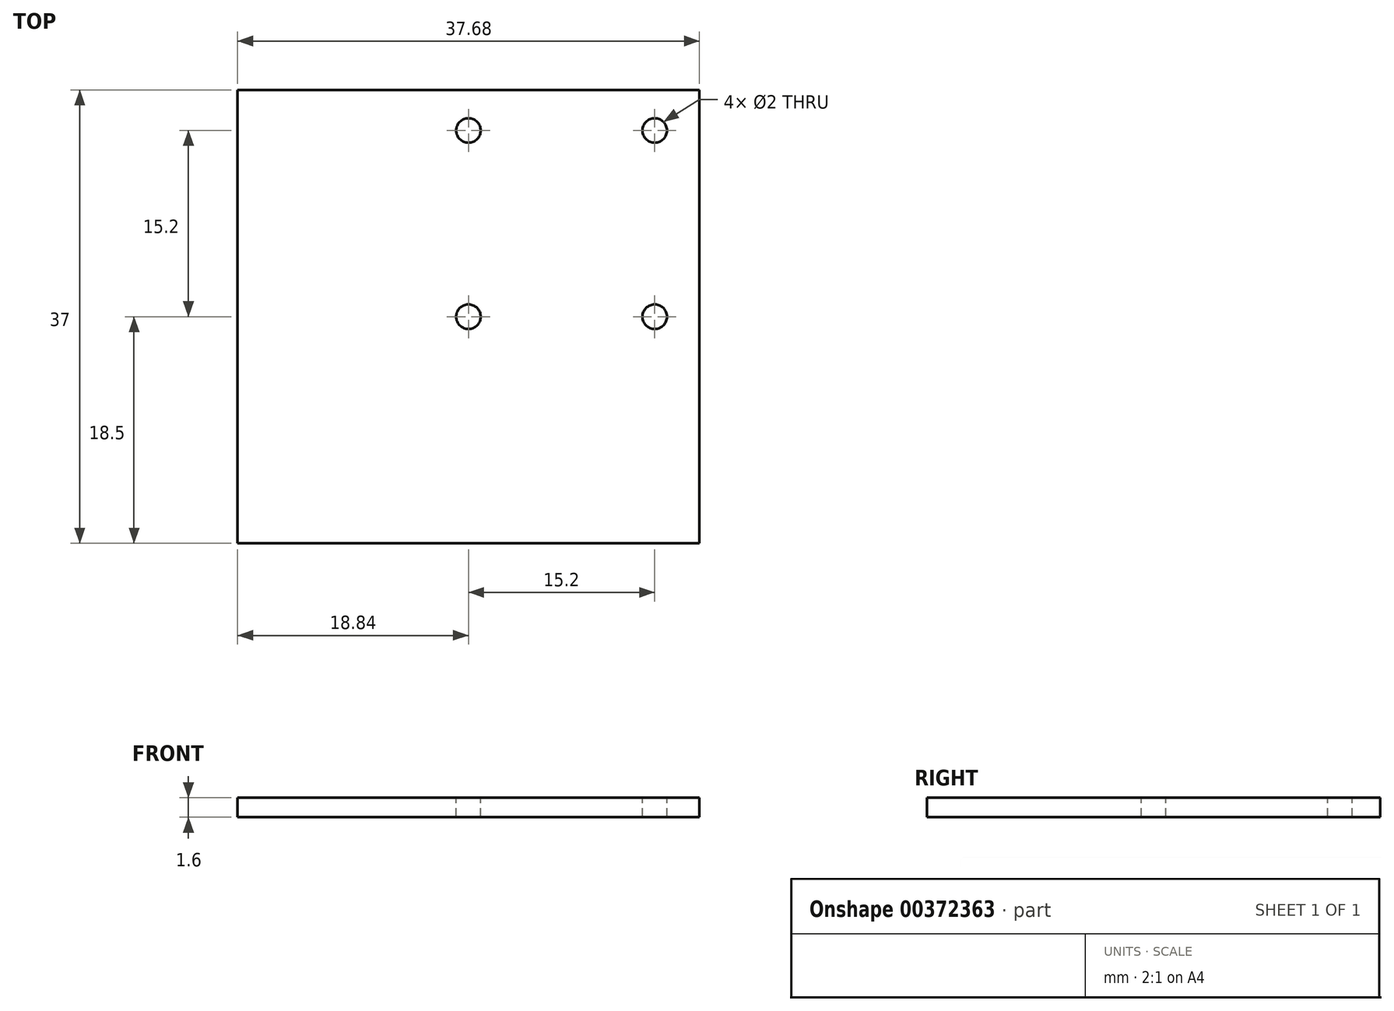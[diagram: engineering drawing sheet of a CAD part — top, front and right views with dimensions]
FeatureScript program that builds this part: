
annotation { "Feature Type Name" : "Feature", "Feature Type Description" : "" }
export const myFeature = defineFeature(function(context is Context, id is Id, definition is map)
    precondition{}
    {
        {
            var Q0;
            Q0=qCreatedBy(makeId("Top.planeOp"),FACE);
            var sketch = newSketch(context, id + "F0", { "sketchPlane" : qUnion([Q0])});
            skLineSegment(sketch, "E0.bottom", {"start": v(18.84, 18.5) * mm, "end": v(-18.84, 18.5) * mm});
            skLineSegment(sketch, "E0.top", {"start": v(18.84, -18.5) * mm, "end": v(-18.84, -18.5) * mm});
            skLineSegment(sketch, "E0.left", {"start": v(18.84, 18.5) * mm, "end": v(18.84, -18.5) * mm});
            skLineSegment(sketch, "E0.right", {"start": v(-18.84, 18.5) * mm, "end": v(-18.84, -18.5) * mm});
            skPoint(sketch, "E0.middle", {"position": v(0, 0) * mm});
            skSolve(sketch);
        }
        {
            var Q0;
            Q0 = qSketchRegion(id + "F0", true);
            extrude(context, id + "F1", {"entities" : qUnion([Q0]), "depth" : 1.6 * mm});
        }
        {
            var Q0;
            Q0=makeQuery(id+"F1.opExtrude","CAP_FACE",FACE,{"disambiguationData":[OSD([sQuery(id+"F0.wireOp",EDGE,"E0.bottom"),sQuery(id+"F0.wireOp",EDGE,"E0.top"),sQuery(id+"F0.wireOp",EDGE,"E0.left"),sQuery(id+"F0.wireOp",EDGE,"E0.right")])],"isStart":false});
            var sketch = newSketch(context, id + "F2", { "sketchPlane" : qUnion([Q0])});
            skCircle(sketch, "E1", {"center": v(0, 0) * mm, "radius": 1 * mm});
            skCircle(sketch, "E2.0.1.0", {"center": v(0, 15.2) * mm, "radius": 1 * mm});
            skCircle(sketch, "E2.1.0.0", {"center": v(15.2, 0) * mm, "radius": 1 * mm});
            skCircle(sketch, "E2.1.1.0", {"center": v(15.2, 15.2) * mm, "radius": 1 * mm});
            skLineSegment(sketch, "E2.direction1", {"start": v(0, 0) * mm, "end": v(15.2, 0) * mm, "construction": true});
            skLineSegment(sketch, "E2.direction2", {"start": v(0, 0) * mm, "end": v(0, 15.2) * mm, "construction": true});
            skSolve(sketch);
        }
        {
            var Q0;
            Q0 = qSketchRegion(id + "F2", true);
            extrude(context, id + "F3", {"entities" : qUnion([Q0]), "operationType" : NewBodyOperationType.REMOVE, "oppositeDirection" : true, "depth" : 25 * mm});
        }
    });
